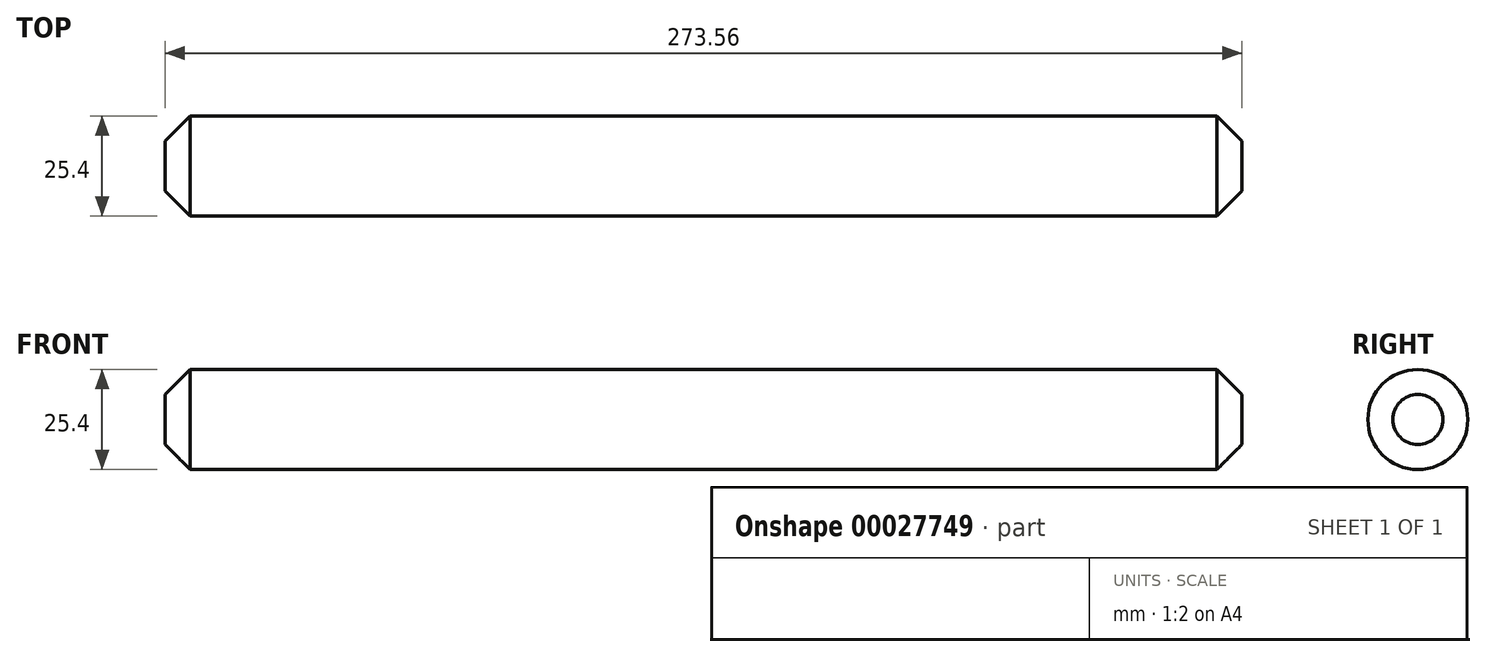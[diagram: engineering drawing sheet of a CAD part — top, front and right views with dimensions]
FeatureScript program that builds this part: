
annotation { "Feature Type Name" : "Feature", "Feature Type Description" : "" }
export const myFeature = defineFeature(function(context is Context, id is Id, definition is map)
    precondition{}
    {
        {
            var Q0;
            Q0=qCreatedBy(makeId("Right.planeOp"),FACE);
            var sketch = newSketch(context, id + "F0", { "sketchPlane" : qUnion([Q0])});
            skCircle(sketch, "E0", {"center": v(0, 0) * mm, "radius": 12.7 * mm});
            skLineSegment(sketch, "E1", {"start": v(-45.5, 23.27) * mm, "end": v(-12.92, 15.93) * mm});
            skLineSegment(sketch, "E2", {"start": v(-12.92, 15.93) * mm, "end": v(-10.57, 26.4) * mm});
            skLineSegment(sketch, "E3", {"start": v(-10.57, 26.4) * mm, "end": v(-85.92, 55.84) * mm});
            skLineSegment(sketch, "E4", {"start": v(-27.34, 32.95) * mm, "end": v(-68.04, 48.85) * mm});
            skSolve(sketch);
        }
        {
            var Q0;
            Q0 = qSketchRegion(id + "F0", true);
            extrude(context, id + "F1", {"entities" : qUnion([Q0]), "endBound" : BoundingType.SYMMETRIC, "depth" : 273.56 * mm});
        }
        {
            var Q0;
            Q0=makeQuery(id+"F1.opExtrude","CAP_EDGE",EDGE,{"disambiguationData":[OSD([sQuery(id+"F0.wireOp",EDGE,"E0")])],"isStart":false});
            var Q1;
            Q1=makeQuery(id+"F1.opExtrude","SWEPT_FACE",FACE,{"disambiguationData":[OSD([sQuery(id+"F0.wireOp",EDGE,"E0")])]});
            chamfer(context, id + "F2", {"entities" : qUnion([Q0, Q1]), "width" : 6.35 * mm, "tangentPropagation" : true});
        }
    });
